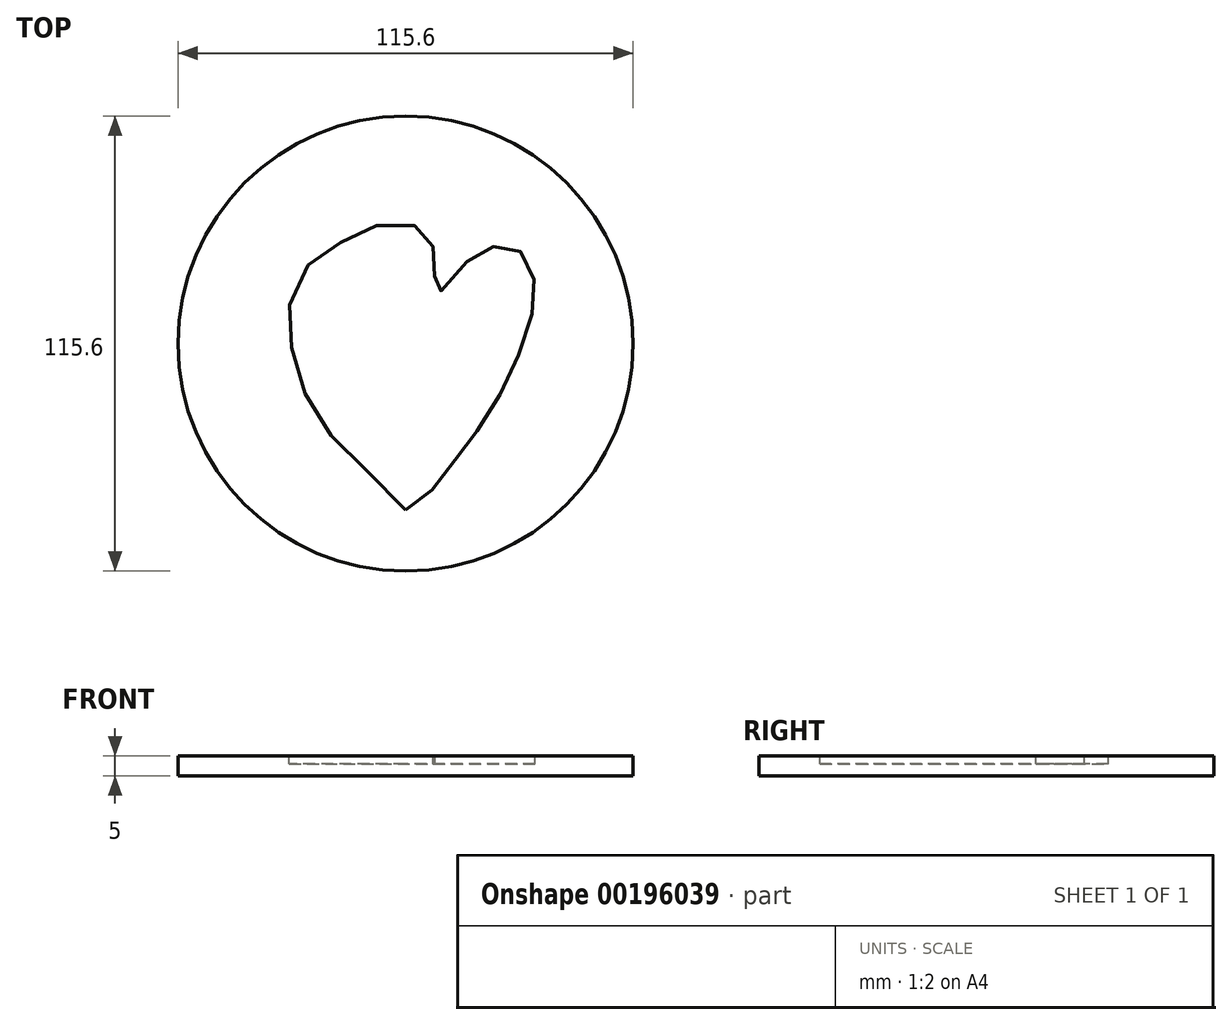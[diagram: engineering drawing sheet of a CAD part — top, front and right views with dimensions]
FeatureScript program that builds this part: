
annotation { "Feature Type Name" : "Feature", "Feature Type Description" : "" }
export const myFeature = defineFeature(function(context is Context, id is Id, definition is map)
    precondition{}
    {
        {
            var Q0;
            Q0=qCreatedBy(makeId("Top.planeOp"),FACE);
            var sketch = newSketch(context, id + "F0", { "sketchPlane" : qUnion([Q0])});
            skCircle(sketch, "E0", {"center": v(0, 0) * mm, "radius": 57.8 * mm});
            skSolve(sketch);
        }
        {
            var Q0;
            Q0 = qSketchRegion(id + "F0", true);
            extrude(context, id + "F1", {"entities" : qUnion([Q0]), "depth" : 5 * mm});
        }
        {
            var Q0;
            Q0=makeQuery(id+"F1.opExtrude","CAP_FACE",FACE,{"disambiguationData":[OSD([sQuery(id+"F0.wireOp",EDGE,"E0")])],"isStart":false});
            var sketch = newSketch(context, id + "F2", { "sketchPlane" : qUnion([Q0])});
            skFitSpline(sketch, "E1", {"points": [v(0, -42.25) * mm, v(-12.63, -29.06) * mm, v(-21.34, -20.64) * mm, v(-27.8, -6.04) * mm, v(-29.48, 3.8) * mm, v(-28.07, 15.3) * mm, v(-20.78, 23.16) * mm, v(-13.76, 27.1) * mm, v(-4.77, 30.74) * mm, v(3.09, 29.62) * mm, v(6.46, 26.25) * mm, v(7.3, 21.76) * mm, v(7.3, 16.14) * mm, v(7.3, 12.5) * mm, v(12.91, 17.55) * mm, v(16.84, 22.04) * mm, v(22.18, 24.57) * mm, v(27.23, 24.57) * mm, v(30.32, 22.04) * mm, v(32.57, 16.42) * mm, v(32.57, 9.97) * mm, v(29.76, 0) * mm, v(25.55, -9.69) * mm, v(19.93, -19.8) * mm, v(14.6, -26.53) * mm, v(10.67, -32.43) * mm, v(4.77, -39.45) * mm, v(0, -42.25) * mm]});
            skSolve(sketch);
        }
        {
            var Q0;
            Q0=makeQuery(id+"F2.imprint","IMPRINT",FACE,{"disambiguationData":[TD([[makeQuery(id+"F2.imprint","IMPRINT",EDGE,{"derivedFrom":sQuery(id+"F2.wireOp",EDGE,"E1")}),-1.0]])]});
            extrude(context, id + "F3", {"entities" : qUnion([Q0]), "operationType" : NewBodyOperationType.REMOVE, "oppositeDirection" : true, "depth" : 2 * mm});
        }
    });
